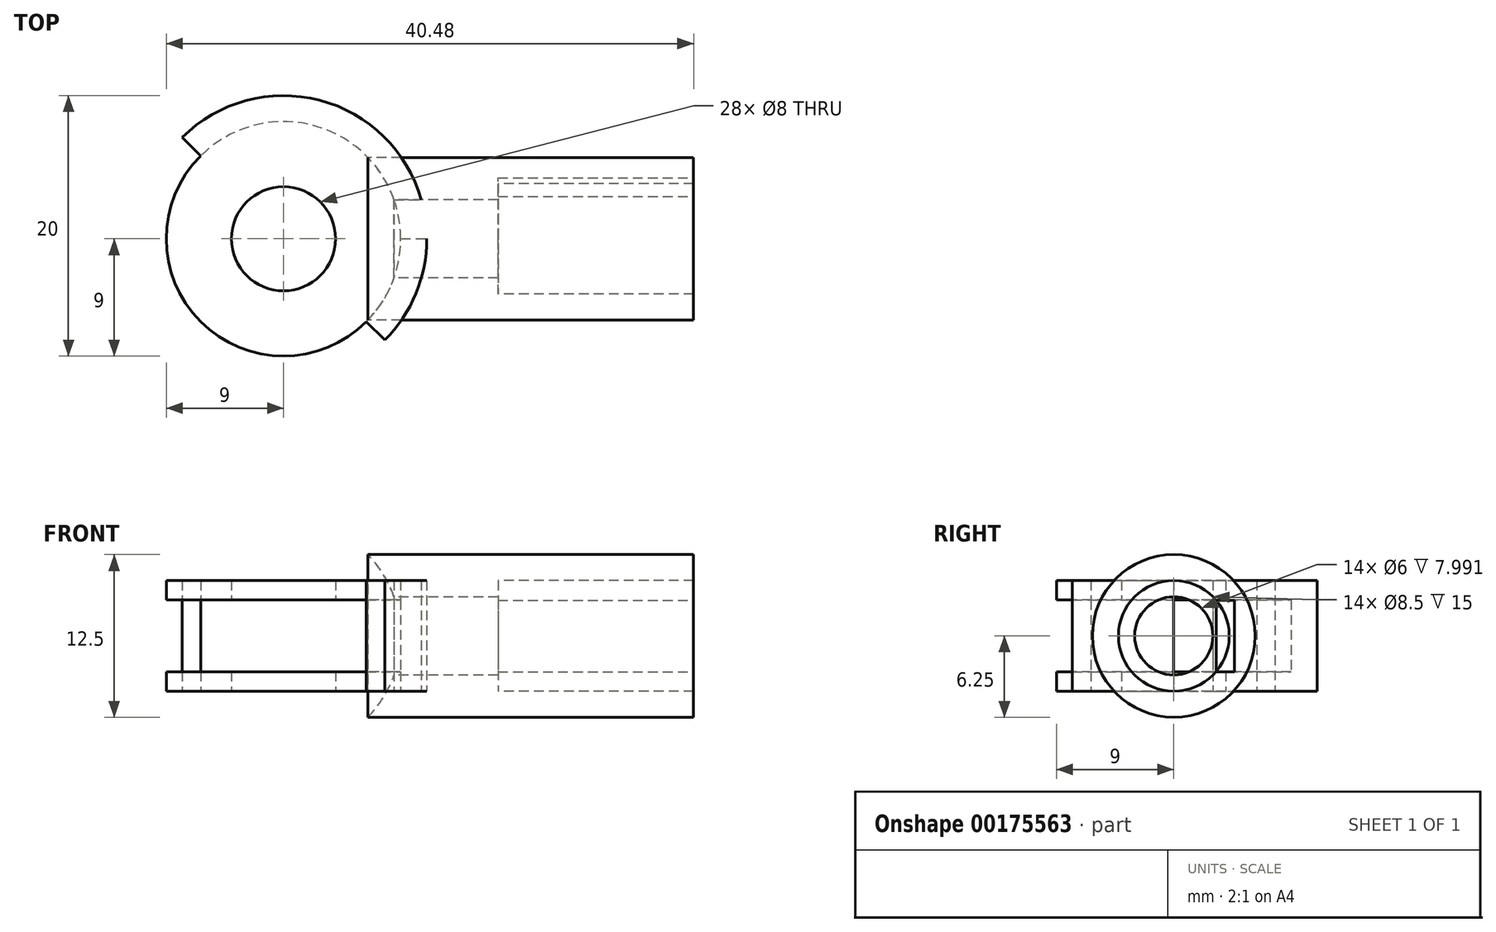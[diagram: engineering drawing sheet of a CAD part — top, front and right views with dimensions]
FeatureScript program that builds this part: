
annotation { "Feature Type Name" : "Feature", "Feature Type Description" : "" }
export const myFeature = defineFeature(function(context is Context, id is Id, definition is map)
    precondition{}
    {
        {
            var Q0;
            Q0=qCreatedBy(makeId("Top.planeOp"),FACE);
            var sketch = newSketch(context, id + "F0", { "sketchPlane" : qUnion([Q0])});
            skCircle(sketch, "E0", {"center": v(0, 0) * mm, "radius": 9 * mm});
            skCircle(sketch, "E1", {"center": v(0, 0) * mm, "radius": 11 * mm});
            skCircle(sketch, "E2", {"center": v(0, 0) * mm, "radius": 4 * mm});
            skLineSegment(sketch, "E3", {"start": v(-11, 11) * mm, "end": v(11, -11) * mm, "construction": true});
            skLineSegment(sketch, "E4", {"start": v(-15.02, 0) * mm, "end": v(40.47, 0) * mm, "construction": true});
            skLineSegment(sketch, "E5", {"start": v(-7.78, 7.78) * mm, "end": v(-6.36, 6.36) * mm});
            skLineSegment(sketch, "E6", {"start": v(6.36, -6.36) * mm, "end": v(7.78, -7.78) * mm});
            skLineSegment(sketch, "E7.MirrorCS", {"start": v(8.49, 3) * mm, "end": v(16.48, 3) * mm});
            skLineSegment(sketch, "E8.MirrorCS", {"start": v(16.48, 4.25) * mm, "end": v(31.48, 4.25) * mm});
            skLineSegment(sketch, "E9.MirrorCS", {"start": v(31.48, 4.25) * mm, "end": v(31.48, 6.25) * mm});
            skLineSegment(sketch, "E10.MirrorCS", {"start": v(31.48, 6.25) * mm, "end": v(6.48, 6.25) * mm});
            skLineSegment(sketch, "E11.MirrorCS", {"start": v(16.48, 3) * mm, "end": v(16.48, 4.25) * mm});
            skLineSegment(sketch, "E12", {"start": v(8.49, 3) * mm, "end": v(-8.49, 3) * mm});
            skLineSegment(sketch, "E13", {"start": v(9, 0) * mm, "end": v(11, 0) * mm});
            skSolve(sketch);
        }
        {
            var Q0;
            {var subQ3=sQuery(id+"F0.wireOp",EDGE,"E10.MirrorCS");var subQ5=sQuery(id+"F0.wireOp",EDGE,"E1");var subQ6=makeQuery(id+"F0.imprint","INTERSECT",VERTEX,{"derivedFrom":[subQ5,subQ3]});Q0=makeQuery(id+"F0.imprint","IMPRINT",FACE,{"disambiguationData":[TD([[makeQuery(id+"F0.imprint","IMPRINT",EDGE,{"disambiguationData":[TD([[subQ6,1.0]])],"derivedFrom":subQ5}),1.0]])]});}
            var Q1;
            Q1=makeQuery(id+"F0.imprint","IMPRINT",FACE,{"disambiguationData":[TD([[makeQuery(id+"F0.imprint","IMPRINT",EDGE,{"derivedFrom":sQuery(id+"F0.wireOp",EDGE,"E8.MirrorCS")}),1.0]])]});
            var Q2;
            Q2=sQuery(id+"F0.wireOp",EDGE,"E4");
            revolve(context, id + "F1", {"entities" : qUnion([Q0, Q1]), "axis" : qUnion([Q2]), "revolveType" : RevolveType.FULL});
        }
        {
            var Q0;
            {var subQ0=sQuery(id+"F0.wireOp",EDGE,"E5");Q0=makeQuery(id+"F0.imprint","IMPRINT",FACE,{"disambiguationData":[TD([[makeQuery(id+"F0.imprint","IMPRINT",EDGE,{"derivedFrom":subQ0}),1.0]])]});}
            var Q1;
            {var subQ3=sQuery(id+"F0.wireOp",EDGE,"E10.MirrorCS");var subQ5=sQuery(id+"F0.wireOp",EDGE,"E1");var subQ6=makeQuery(id+"F0.imprint","INTERSECT",VERTEX,{"derivedFrom":[subQ5,subQ3]});Q1=makeQuery(id+"F0.imprint","IMPRINT",FACE,{"disambiguationData":[TD([[makeQuery(id+"F0.imprint","IMPRINT",EDGE,{"disambiguationData":[TD([[subQ6,1.0]])],"derivedFrom":subQ5}),1.0]])]});}
            var Q2;
            {var subQ0=sQuery(id+"F0.wireOp",EDGE,"E6");Q2=makeQuery(id+"F0.imprint","IMPRINT",FACE,{"disambiguationData":[TD([[makeQuery(id+"F0.imprint","IMPRINT",EDGE,{"derivedFrom":subQ0}),1.0]])]});}
            var Q3;
            {var subQ4=sQuery(id+"F0.wireOp",EDGE,"E0");var subQ5=makeQuery(id+"F0.imprint","INTERSECT",VERTEX,{"derivedFrom":[subQ4,sQuery(id+"F0.wireOp",EDGE,"E6")]});Q3=makeQuery(id+"F0.imprint","IMPRINT",FACE,{"disambiguationData":[TD([[makeQuery(id+"F0.imprint","IMPRINT",EDGE,{"disambiguationData":[TD([[subQ5,1.0]])],"derivedFrom":subQ4}),1.0]])]});}
            var Q4;
            {var subQ4=sQuery(id+"F0.wireOp",EDGE,"E0");var subQ5=makeQuery(id+"F0.imprint","INTERSECT",VERTEX,{"derivedFrom":[subQ4,sQuery(id+"F0.wireOp",EDGE,"E5")]});Q4=makeQuery(id+"F0.imprint","IMPRINT",FACE,{"disambiguationData":[TD([[makeQuery(id+"F0.imprint","IMPRINT",EDGE,{"disambiguationData":[TD([[subQ5,1.0]])],"derivedFrom":subQ4}),1.0]])]});}
            var Q5;
            {var subQ3=sQuery(id+"F0.wireOp",EDGE,"8NYlZVcY-SoaZ-VYeR-GlyI-CV0pEvSKxlMz");Q5=makeQuery(id+"F0.imprint","IMPRINT",FACE,{"disambiguationData":[TD([[makeQuery(id+"F0.imprint","IMPRINT",EDGE,{"derivedFrom":subQ3}),1.0]])]});}
            extrude(context, id + "F2", {"entities" : qUnion([Q0, Q1, Q2, Q3, Q4, Q5]), "depth" : 8.5 * mm, "symmetric" : true});
        }
        {
            var Q0;
            Q0=makeQuery(id+"F0.imprint","IMPRINT",FACE,{"disambiguationData":[TD([[makeQuery(id+"F0.imprint","IMPRINT",EDGE,{"derivedFrom":sQuery(id+"F0.wireOp",EDGE,"E2")}),1.0]])]});
            var Q1;
            Q1=makeQuery(id+"F0.imprint","IMPRINT",FACE,{"disambiguationData":[TD([[makeQuery(id+"F0.imprint","IMPRINT",EDGE,{"derivedFrom":sQuery(id+"F0.wireOp",EDGE,"E2")}),-1.0]])]});
            extrude(context, id + "F3", {"entities" : qUnion([Q0, Q1]), "depth" : 5.5 * mm, "symmetric" : true});
        }
        {
            var Q0;
            Q0=makeQuery(id+"F3.opExtrude","SWEPT_BODY",BODY,{"disambiguationData":[OSD([sQuery(id+"F0.wireOp",EDGE,"E0"),sQuery(id+"F0.wireOp",EDGE,"E2"),sQuery(id+"F0.wireOp",EDGE,"E12")])]});
            var Q1;
            Q1=makeQuery(id+"F2.opExtrude","SWEPT_BODY",BODY,{"disambiguationData":[OSD([sQuery(id+"F0.wireOp",EDGE,"E0"),sQuery(id+"F0.wireOp",EDGE,"E1"),sQuery(id+"F0.wireOp",EDGE,"E2"),sQuery(id+"F0.wireOp",EDGE,"E5"),sQuery(id+"F0.wireOp",EDGE,"E6")])]});
            booleanBodies(context, id + "F4", {"operationType" : BooleanOperationType.SUBTRACTION, "tools" : qUnion([Q0]), "targets" : qUnion([Q1])});
        }
        {
            var Q0;
            Q0=makeQuery(id+"F2.opExtrude","CAP_FACE",FACE,{"disambiguationData":[OSD([sQuery(id+"F0.wireOp",EDGE,"E0"),sQuery(id+"F0.wireOp",EDGE,"E1"),sQuery(id+"F0.wireOp",EDGE,"E2"),sQuery(id+"F0.wireOp",EDGE,"E5"),sQuery(id+"F0.wireOp",EDGE,"E6")])],"isStart":false});
            var sketch = newSketch(context, id + "F5", { "sketchPlane" : qUnion([Q0])});
            skLineSegment(sketch, "E14.bottom", {"start": v(15.36, 8.97) * mm, "end": v(6.36, 8.97) * mm});
            skLineSegment(sketch, "E14.top", {"start": v(15.36, -6.36) * mm, "end": v(6.36, -6.36) * mm});
            skLineSegment(sketch, "E14.left", {"start": v(15.36, 8.97) * mm, "end": v(15.36, -6.36) * mm});
            skLineSegment(sketch, "E14.right", {"start": v(6.36, 8.97) * mm, "end": v(6.36, -6.36) * mm});
            skSolve(sketch);
        }
        {
            var Q0;
            Q0 = qSketchRegion(id + "F5", true);
            extrude(context, id + "F6", {"entities" : qUnion([Q0]), "depth" : 3 * mm});
        }
        {
            var Q0;
            Q0=makeQuery(id+"F2.opExtrude","CAP_FACE",FACE,{"disambiguationData":[OSD([sQuery(id+"F0.wireOp",EDGE,"E0"),sQuery(id+"F0.wireOp",EDGE,"E1"),sQuery(id+"F0.wireOp",EDGE,"E2"),sQuery(id+"F0.wireOp",EDGE,"E5"),sQuery(id+"F0.wireOp",EDGE,"E6")])],"isStart":true});
            var sketch = newSketch(context, id + "F7", { "sketchPlane" : qUnion([Q0])});
            skLineSegment(sketch, "E15.bottom", {"start": v(6.36, 6.36) * mm, "end": v(15.36, 6.36) * mm});
            skLineSegment(sketch, "E15.top", {"start": v(6.36, -9.05) * mm, "end": v(15.36, -9.05) * mm});
            skLineSegment(sketch, "E15.left", {"start": v(6.36, 6.36) * mm, "end": v(6.36, -9.05) * mm});
            skLineSegment(sketch, "E15.right", {"start": v(15.36, 6.36) * mm, "end": v(15.36, -9.05) * mm});
            skSolve(sketch);
        }
        {
            var Q0;
            Q0=makeQuery(id+"F1.opRevolve","SWEPT_FACE",FACE,{"disambiguationData":[OSD([sQuery(id+"F0.wireOp",EDGE,"E9.MirrorCS")])]});
            var sketch = newSketch(context, id + "F8", { "sketchPlane" : qUnion([Q0])});
            skLineSegment(sketch, "E16", {"start": v(3.25, 2.74) * mm, "end": v(3.25, -2.74) * mm});
            skLineSegment(sketch, "E17.bottom", {"start": v(3.25, 2.74) * mm, "end": v(4.67, 2.74) * mm});
            skLineSegment(sketch, "E17.top", {"start": v(3.25, -2.77) * mm, "end": v(4.67, -2.77) * mm});
            skLineSegment(sketch, "E17.left", {"start": v(3.25, 2.74) * mm, "end": v(3.25, -2.77) * mm});
            skLineSegment(sketch, "E17.right", {"start": v(4.67, 2.74) * mm, "end": v(4.67, -2.77) * mm});
            skSolve(sketch);
        }
        {
            var Q0;
            Q0 = qSketchRegion(id + "F8", true);
            var Q1;
            Q1=makeQuery(id+"F1.opRevolve","SWEPT_FACE",FACE,{"disambiguationData":[OSD([sQuery(id+"F0.wireOp",EDGE,"E11.MirrorCS")])]});
            extrude(context, id + "F9", {"entities" : qUnion([Q0]), "endBound" : BoundingType.UP_TO_SURFACE, "oppositeDirection" : true, "endBoundEntityFace" : qUnion([Q1]), "depth" : 25 * mm});
        }
        {
            var Q0;
            Q0 = qSketchRegion(id + "F7", true);
            extrude(context, id + "F10", {"entities" : qUnion([Q0]), "depth" : 2.5 * mm});
        }
        {
            var Q0;
            Q0=makeQuery(id+"F6.opExtrude","SWEPT_BODY",BODY,{"disambiguationData":[OSD([sQuery(id+"F5.wireOp",EDGE,"E14.bottom"),sQuery(id+"F5.wireOp",EDGE,"E14.top"),sQuery(id+"F5.wireOp",EDGE,"E14.left"),sQuery(id+"F5.wireOp",EDGE,"E14.right")])]});
            var Q1;
            Q1=makeQuery(id+"F10.opExtrude","SWEPT_BODY",BODY,{"disambiguationData":[OSD([sQuery(id+"F7.wireOp",EDGE,"E15.bottom"),sQuery(id+"F7.wireOp",EDGE,"E15.top"),sQuery(id+"F7.wireOp",EDGE,"E15.left"),sQuery(id+"F7.wireOp",EDGE,"E15.right")])]});
            var Q2;
            Q2=makeQuery(id+"F2.opExtrude","SWEPT_BODY",BODY,{"disambiguationData":[OSD([sQuery(id+"F0.wireOp",EDGE,"E0"),sQuery(id+"F0.wireOp",EDGE,"E1"),sQuery(id+"F0.wireOp",EDGE,"E2"),sQuery(id+"F0.wireOp",EDGE,"E5"),sQuery(id+"F0.wireOp",EDGE,"E6")])]});
            booleanBodies(context, id + "F11", {"operationType" : BooleanOperationType.SUBTRACTION, "tools" : qUnion([Q0, Q1]), "targets" : qUnion([Q2])});
        }
    });
